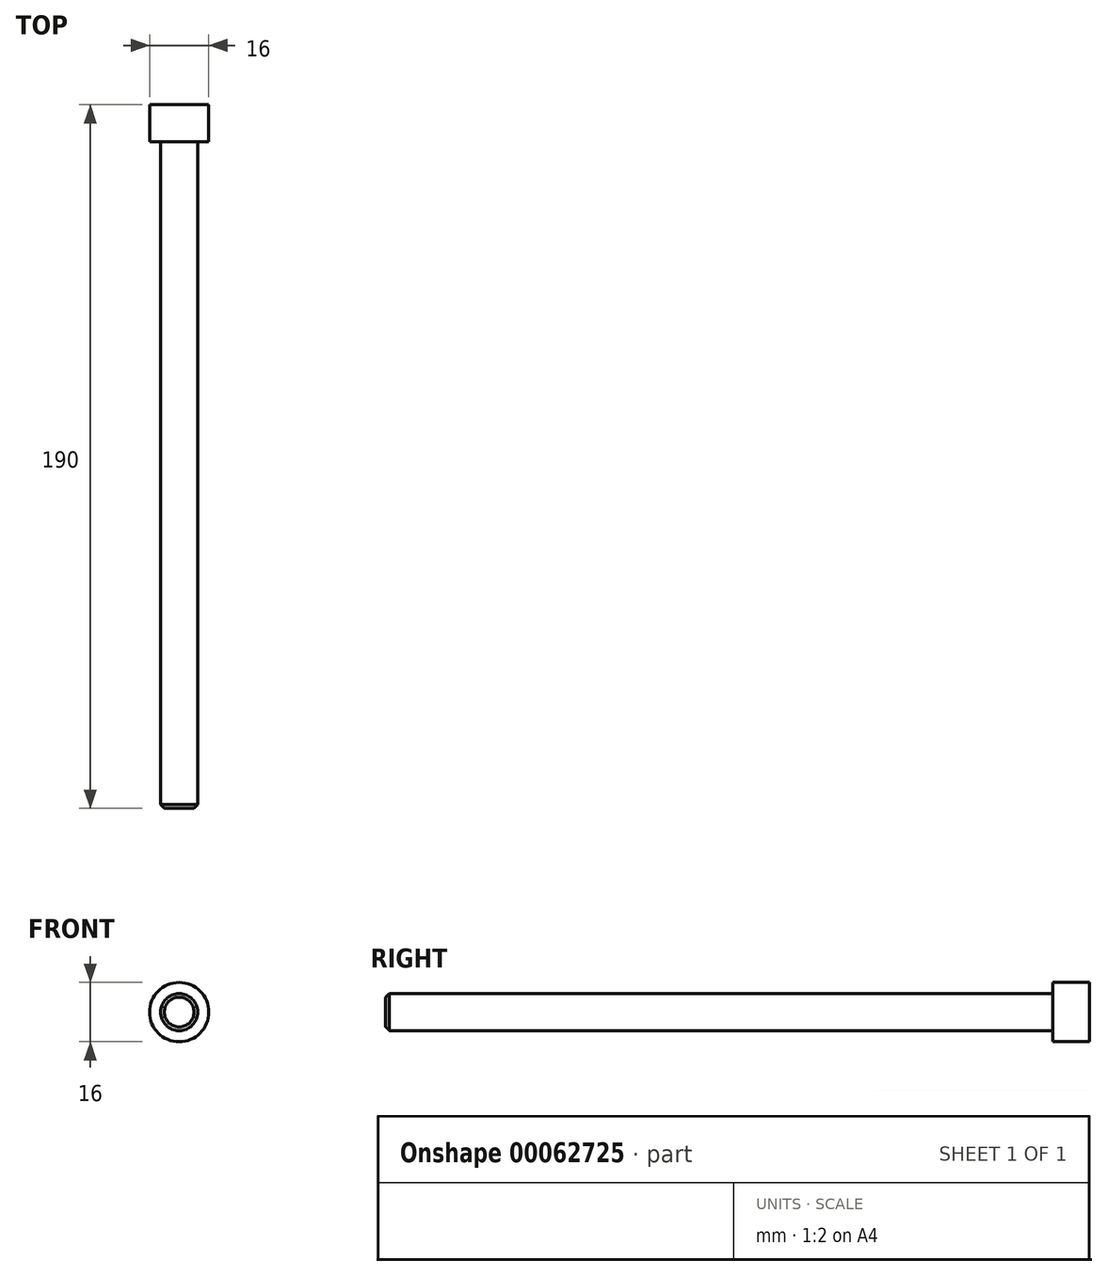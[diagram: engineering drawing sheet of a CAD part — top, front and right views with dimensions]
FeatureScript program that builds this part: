
annotation { "Feature Type Name" : "Feature", "Feature Type Description" : "" }
export const myFeature = defineFeature(function(context is Context, id is Id, definition is map)
    precondition{}
    {
        {
            var Q0;
            Q0=qCreatedBy(makeId("Front.planeOp"),FACE);
            var sketch = newSketch(context, id + "F0", { "sketchPlane" : qUnion([Q0])});
            skCircle(sketch, "E0", {"center": v(0, 0) * mm, "radius": 8 * mm});
            skCircle(sketch, "E1", {"center": v(0, 0) * mm, "radius": 5 * mm});
            skSolve(sketch);
        }
        {
            var Q0;
            Q0=makeQuery(id+"F0.imprint","IMPRINT",FACE,{"disambiguationData":[TD([[makeQuery(id+"F0.imprint","IMPRINT",EDGE,{"derivedFrom":sQuery(id+"F0.wireOp",EDGE,"E1")}),1.0]])]});
            var Q1;
            Q1=makeQuery(id+"F0.imprint","IMPRINT",FACE,{"disambiguationData":[TD([[makeQuery(id+"F0.imprint","IMPRINT",EDGE,{"derivedFrom":sQuery(id+"F0.wireOp",EDGE,"E0")}),1.0]])]});
            extrude(context, id + "F1", {"entities" : qUnion([Q0, Q1]), "oppositeDirection" : true, "depth" : 10 * mm});
        }
        {
            var Q0;
            Q0=makeQuery(id+"F0.imprint","IMPRINT",FACE,{"disambiguationData":[TD([[makeQuery(id+"F0.imprint","IMPRINT",EDGE,{"derivedFrom":sQuery(id+"F0.wireOp",EDGE,"E1")}),1.0]])]});
            extrude(context, id + "F2", {"entities" : qUnion([Q0]), "operationType" : NewBodyOperationType.ADD, "depth" : 180 * mm});
        }
        {
            var Q0;
            Q0=makeQuery(id+"F2.opExtrude","CAP_EDGE",EDGE,{"disambiguationData":[OSD([sQuery(id+"F0.wireOp",EDGE,"E1")])],"isStart":false});
            chamfer(context, id + "F3", {"entities" : qUnion([Q0]), "width" : 1 * mm, "tangentPropagation" : true});
        }
    });
